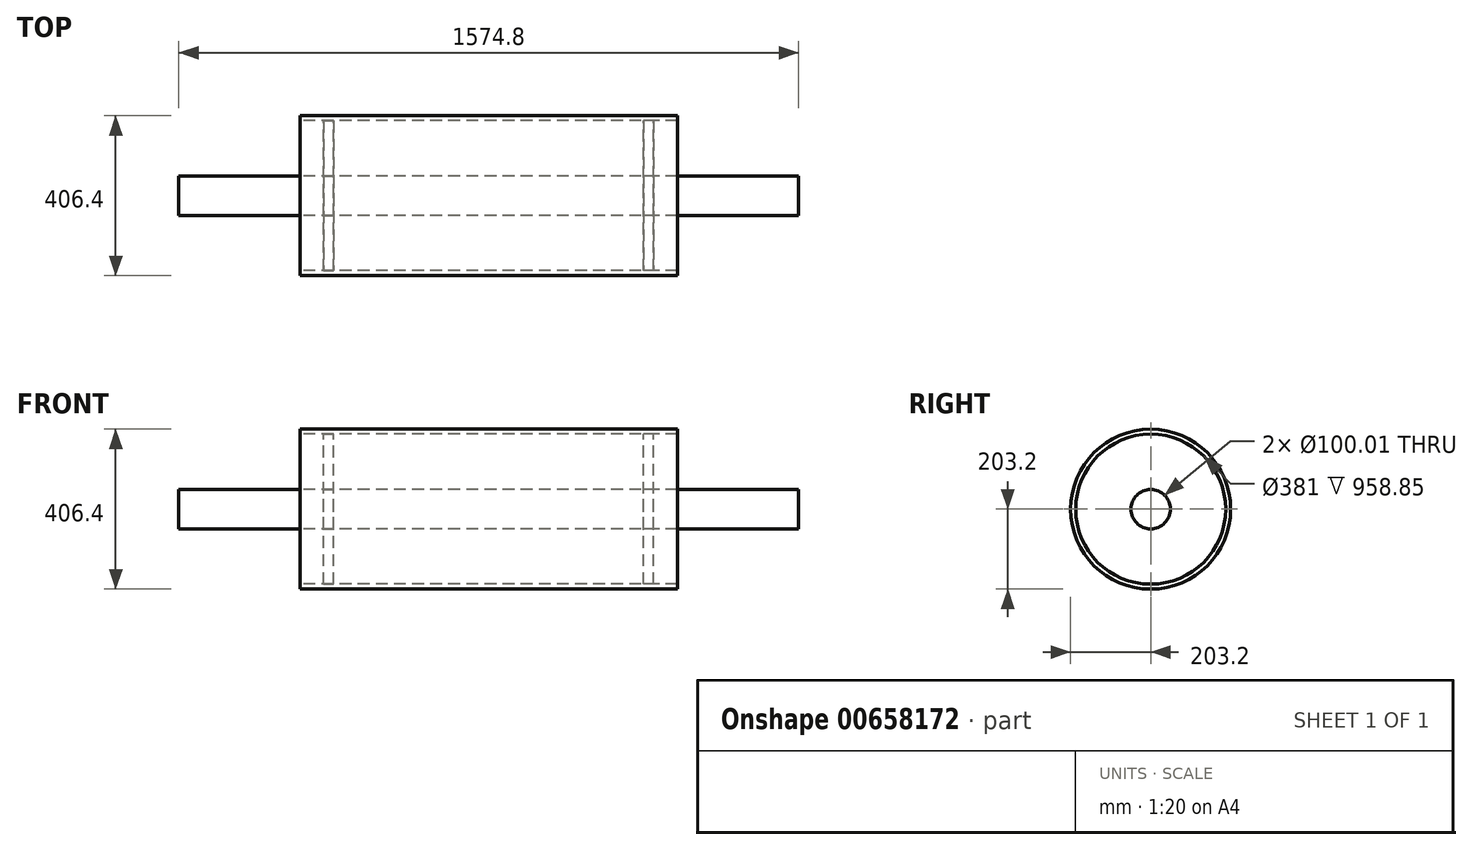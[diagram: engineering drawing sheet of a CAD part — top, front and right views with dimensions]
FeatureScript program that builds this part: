
annotation { "Feature Type Name" : "Feature", "Feature Type Description" : "" }
export const myFeature = defineFeature(function(context is Context, id is Id, definition is map)
    precondition{}
    {
        {
            var Q0;
            Q0=qCreatedBy(makeId("Right.planeOp"),FACE);
            var sketch = newSketch(context, id + "F0", { "sketchPlane" : qUnion([Q0])});
            skCircle(sketch, "E0", {"center": v(0, 0) * mm, "radius": 50 * mm});
            skCircle(sketch, "E1", {"center": v(0, 0) * mm, "radius": 203.2 * mm});
            skCircle(sketch, "E2.0", {"center": v(0, 0) * mm, "radius": 190.5 * mm});
            skSolve(sketch);
        }
        {
            var Q0;
            Q0 = qSketchRegion(id + "F0", true);
            extrude(context, id + "F1", {"entities" : qUnion([Q0]), "endBound" : BoundingType.SYMMETRIC, "depth" : 958.85 * mm, "offsetDistance" : 25.4 * mm});
        }
        {
            var Q0;
            Q0=makeQuery(id+"F0.imprint","IMPRINT",FACE,{"disambiguationData":[TD([[makeQuery(id+"F0.imprint","IMPRINT",EDGE,{"derivedFrom":sQuery(id+"F0.wireOp",EDGE,"E0")}),1.0]])]});
            extrude(context, id + "F2", {"entities" : qUnion([Q0]), "endBound" : BoundingType.SYMMETRIC, "depth" : 1574.8 * mm, "offsetDistance" : 25.4 * mm});
        }
        {
            var Q0;
            Q0=makeQuery(id+"F0.imprint","IMPRINT",FACE,{"disambiguationData":[TD([[makeQuery(id+"F0.imprint","IMPRINT",EDGE,{"derivedFrom":sQuery(id+"F0.wireOp",EDGE,"E0")}),-1.0]])]});
            extrude(context, id + "F3", {"entities" : qUnion([Q0]), "depth" : 419.1 * mm, "offsetDistance" : 25.4 * mm, "hasSecondDirection" : true, "secondDirectionOppositeDirection" : false, "secondDirectionDepth" : 393.7 * mm});
        }
        {
            var Q0;
            Q0=makeQuery(id+"F0.imprint","IMPRINT",FACE,{"disambiguationData":[TD([[makeQuery(id+"F0.imprint","IMPRINT",EDGE,{"derivedFrom":sQuery(id+"F0.wireOp",EDGE,"E0")}),-1.0]])]});
            extrude(context, id + "F4", {"entities" : qUnion([Q0]), "oppositeDirection" : true, "depth" : 419.1 * mm, "offsetDistance" : 25.4 * mm, "hasSecondDirection" : true, "secondDirectionOppositeDirection" : true, "secondDirectionDepth" : 393.7 * mm});
        }
    });
